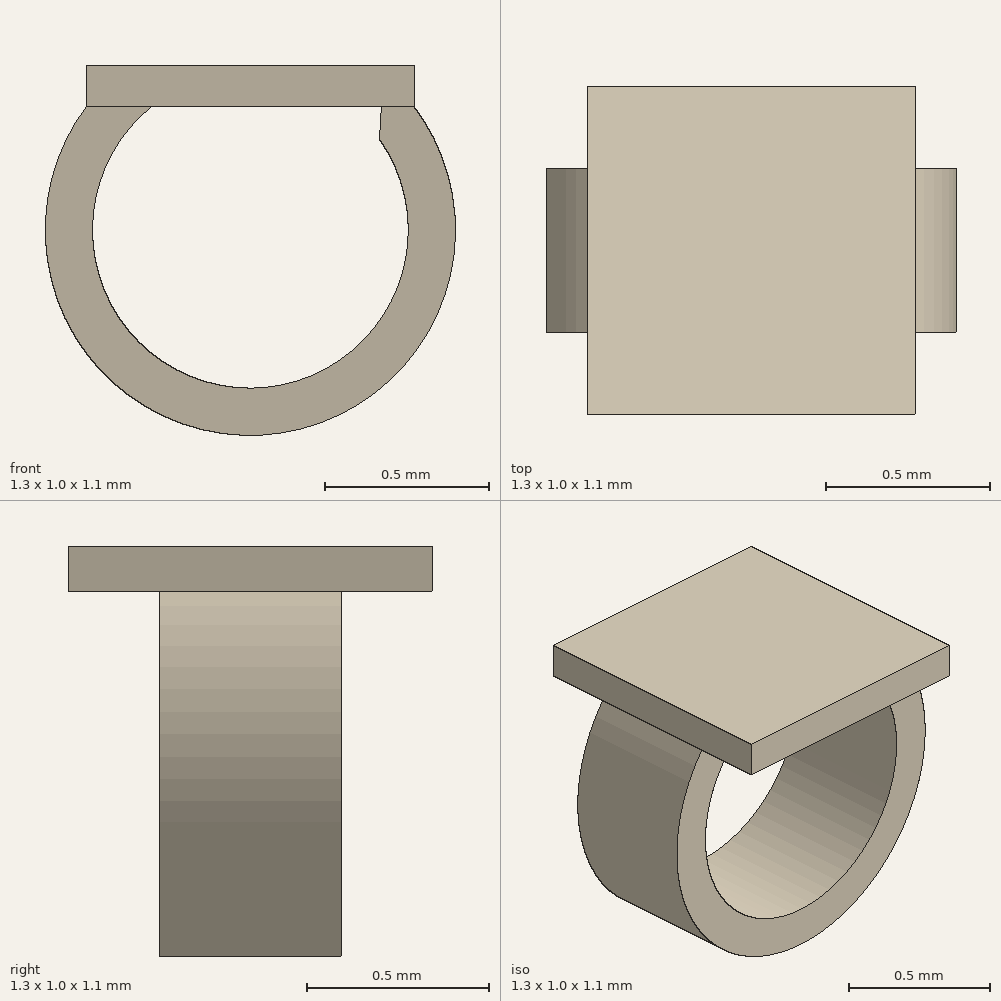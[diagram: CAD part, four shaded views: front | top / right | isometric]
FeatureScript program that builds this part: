
annotation { "Feature Type Name" : "Feature", "Feature Type Description" : "" }
export const myFeature = defineFeature(function(context is Context, id is Id, definition is map)
    precondition{}
    {
        {
            var Q0;
            Q0=qCreatedBy(makeId("Top.planeOp"),FACE);
            var sketch = newSketch(context, id + "F0", { "sketchPlane" : qUnion([Q0])});
            skLineSegment(sketch, "E0.bottom", {"start": v(0.5, -0.5) * mm, "end": v(-0.5, -0.5) * mm});
            skLineSegment(sketch, "E0.top", {"start": v(0.5, 0.5) * mm, "end": v(-0.5, 0.5) * mm});
            skLineSegment(sketch, "E0.left", {"start": v(0.5, -0.5) * mm, "end": v(0.5, 0.5) * mm});
            skLineSegment(sketch, "E0.right", {"start": v(-0.5, -0.5) * mm, "end": v(-0.5, 0.5) * mm});
            skPoint(sketch, "E0.middle", {"position": v(0, 0) * mm});
            skSolve(sketch);
        }
        {
            var Q0;
            Q0=makeQuery(id+"F0.imprint","IMPRINT",FACE,{"disambiguationData":[TD([[makeQuery(id+"F0.imprint","IMPRINT",EDGE,{"derivedFrom":sQuery(id+"F0.wireOp",EDGE,"E0.bottom")}),-1.0]])]});
            extrude(context, id + "F1", {"entities" : qUnion([Q0]), "depth" : 0.12 * mm, "offsetDistance" : 25 * mm});
        }
        {
            var Q0;
            Q0=qCreatedBy(makeId("Front.planeOp"),FACE);
            var sketch = newSketch(context, id + "F2", { "sketchPlane" : qUnion([Q0])});
            skArc(sketch, "E1", {"start": v(-0.4, 0) * mm, "mid": v(0, -0.93) * mm, "end": v(0.4, 0) * mm});
            skSolve(sketch);
        }
        {
            var Q0;
            Q0=makeQuery(id+"F1.opExtrude","CAP_FACE",FACE,{"disambiguationData":[OSD([sQuery(id+"F0.wireOp",EDGE,"E0.bottom"),sQuery(id+"F0.wireOp",EDGE,"E0.top"),sQuery(id+"F0.wireOp",EDGE,"E0.left"),sQuery(id+"F0.wireOp",EDGE,"E0.right")])],"isStart":true});
            var sketch = newSketch(context, id + "F3", { "sketchPlane" : qUnion([Q0])});
            skLineSegment(sketch, "E2.bottom", {"start": v(-0.5, -0.25) * mm, "end": v(-0.3, -0.25) * mm});
            skLineSegment(sketch, "E2.top", {"start": v(-0.5, 0.25) * mm, "end": v(-0.3, 0.25) * mm});
            skLineSegment(sketch, "E2.left", {"start": v(-0.5, -0.25) * mm, "end": v(-0.5, 0.25) * mm});
            skLineSegment(sketch, "E2.right", {"start": v(-0.3, -0.25) * mm, "end": v(-0.3, 0.25) * mm});
            skPoint(sketch, "E2.middle", {"position": v(-0.4, 0) * mm});
            skSolve(sketch);
        }
        {
            var Q0;
            Q0=makeQuery(id+"F3.imprint","IMPRINT",FACE,{"disambiguationData":[TD([[makeQuery(id+"F3.imprint","IMPRINT",EDGE,{"derivedFrom":sQuery(id+"F3.wireOp",EDGE,"E2.bottom")}),1.0]])]});
            var Q1;
            Q1 = qConstructionFilter(qBodyType(qCreatedBy(id + "F2" ,EDGE), BodyType.WIRE), ConstructionObject.NO);
            sweep(context, id + "F4", {"profiles" : qUnion([Q0]), "path" : qUnion([Q1])});
        }
    });
